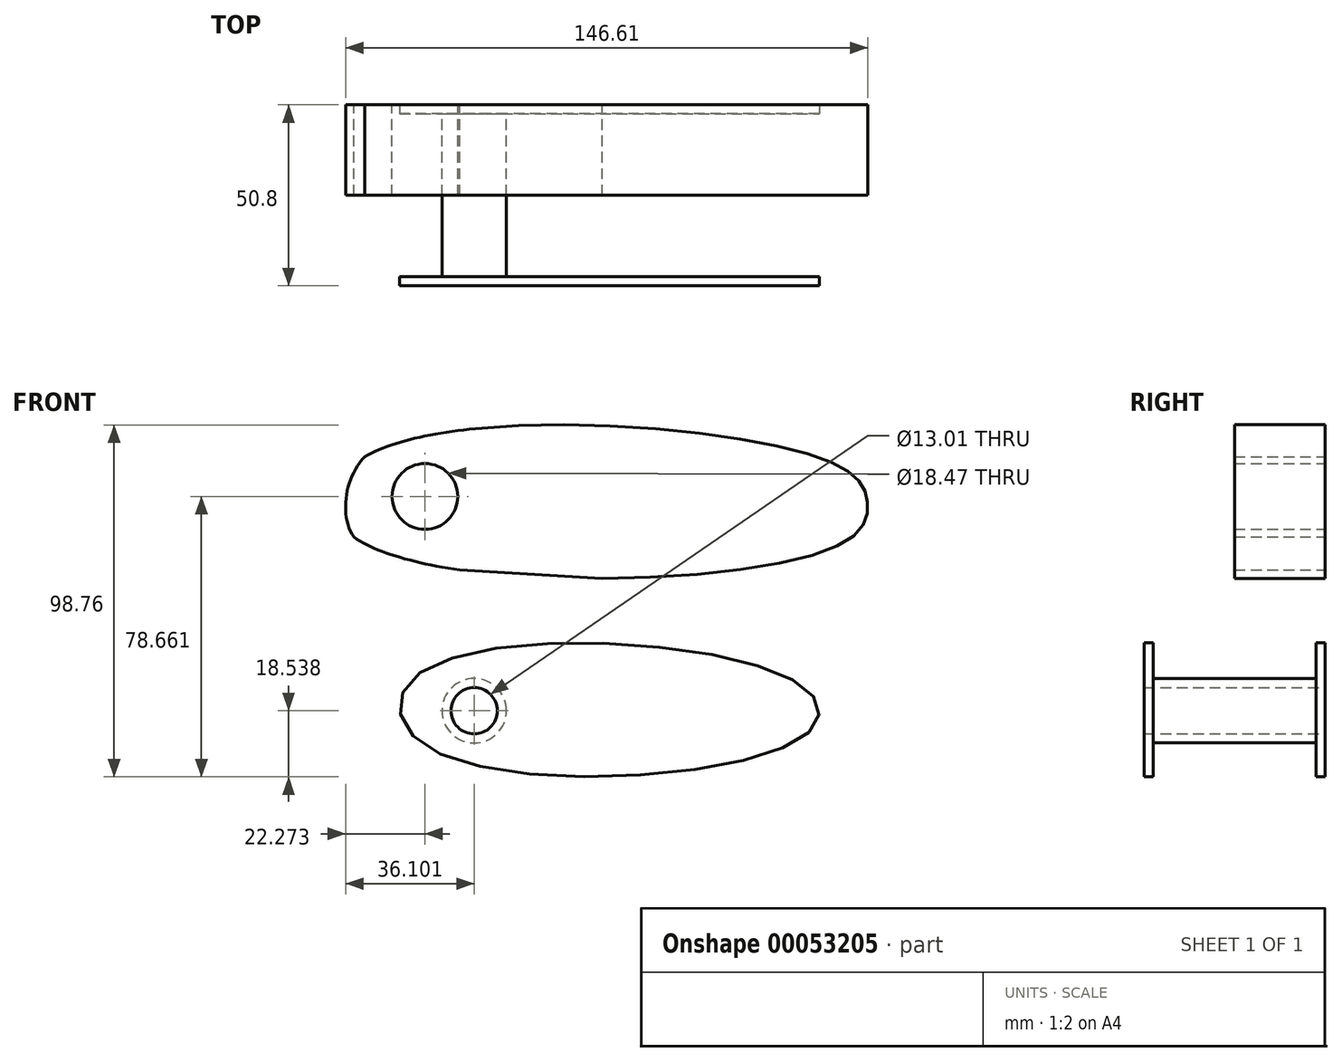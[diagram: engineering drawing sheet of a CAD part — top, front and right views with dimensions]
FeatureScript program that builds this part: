
annotation { "Feature Type Name" : "Feature", "Feature Type Description" : "" }
export const myFeature = defineFeature(function(context is Context, id is Id, definition is map)
    precondition{}
    {
        {
            var Q0;
            Q0=qCreatedBy(makeId("Front.planeOp"),FACE);
            var sketch = newSketch(context, id + "F0", { "sketchPlane" : qUnion([Q0])});
            skFitSpline(sketch, "E0", {"points": [v(-68.42, 42.44) * mm, v(59.76, 42) * mm, v(72.76, 29.88) * mm, v(63.23, 16.89) * mm, v(-71.46, 19.92) * mm, v(-68.42, 42.44) * mm]});
            skFitSpline(sketch, "E1", {"points": [v(-52.83, -18.19) * mm, v(52.83, -20.79) * mm, v(55, -35.94) * mm, v(-50.24, -39.4) * mm, v(-52.83, -18.19) * mm]});
            skFitSpline(sketch, "E2", {"points": [v(-37.3, 50.3) * mm, v(-68.42, 42.44) * mm, v(-71.46, 19.92) * mm, v(-41.68, 10.66) * mm], "startDerivative": vector(-103.97, -3.7) * mm, "endDerivative": vector(107.57, -9.1) * mm});
            skCircle(sketch, "E3", {"center": v(-51.48, 31.27) * mm, "radius": 9.23 * mm});
            skArc(sketch, "E4.trimOffspring", {"start": v(-47.73, 22.83) * mm, "mid": v(-48.92, 22.5) * mm, "end": v(-50.1, 22.14) * mm});
            skFitSpline(sketch, "E5", {"points": [v(-1.76, 8.24) * mm, v(-41.68, 10.66) * mm], "startDerivative": vector(-39.92, 2.42) * mm, "endDerivative": vector(-39.92, 2.42) * mm});
            skCircle(sketch, "E6", {"center": v(-37.65, -28.85) * mm, "radius": 6.5 * mm});
            skSolve(sketch);
        }
        {
            var Q0;
            Q0=makeQuery(id+"F0.imprint","IMPRINT",FACE,{"disambiguationData":[TD([[makeQuery(id+"F0.imprint","IMPRINT",EDGE,{"derivedFrom":sQuery(id+"F0.wireOp",EDGE,"E0")}),-1.0]])]});
            extrude(context, id + "F1", {"entities" : qUnion([Q0]), "depth" : 25.4 * mm});
        }
        {
            var Q0;
            Q0=makeQuery(id+"F0.imprint","IMPRINT",FACE,{"disambiguationData":[TD([[makeQuery(id+"F0.imprint","IMPRINT",EDGE,{"derivedFrom":sQuery(id+"F0.wireOp",EDGE,"E1")}),-1.0]])]});
            extrude(context, id + "F2", {"entities" : qUnion([Q0]), "depth" : 50.8 * mm});
        }
        {
            var Q0;
            Q0=makeQuery(id+"F2.opExtrude","SWEPT_FACE",FACE,{"disambiguationData":[OSD([sQuery(id+"F0.wireOp",EDGE,"E1")])]});
            shell(context, id + "F3", {"entities" : qUnion([Q0]), "thickness" : 2.54 * mm});
        }
    });
